# Revit family: P500296-009
name_source: partatom
category: Lighting Fixtures
units: mm (PartAtom-declared; Revit-internal decimal feet)

## family parameters
Cut with Voids When Loaded = No
Host = Face
Light Source = No
OmniClass Number = 23.80.70.11.14.17
OmniClass Title = Direct/Indirect
Part Type = Normal
Room Calculation Point = No
Round Connector Dimension = Use Diameter
Shared = Yes

## types (1)
- P500296-009
    Apparent Load = 60 VA
    Assembly Code = D5020200
    Connector Description = Lighting Connector
    Default Elevation = 48 "
    Description = Vinings Collection Three-Light Brushed Nickel and Grey Washed Oak Foyer Pendant Light
    Features = Application: Add a touch of casual charm with the Vinings Collection 3-Light Brushed Nickel Coastal Foyer Pendant Light ideal for any foyer, dining room, stairway, or entryway.
Styles: Perfect for farmhouse, coastal, and transitional style settings.
Finish: The chic frame with graceful curving arms is coated in a beautiful brushed nickel finish accented by an ornamental, hand-painted gray washed oak faux wood band.
Materials: Constructed from steel to ensure a long product lifespan.
Glass/Shades: Light sources gather at the center for airy illumination.
Bulbs: For ideal illumination, use 3 candelabra base bulbs that are sold separately (60w max - LED/CFL/incandescent). Compatible with dimmable bulbs.
Dimensions: Measures 15-3/4-inch diameter by 19-1/2-inch height.
Certifications: cETLus dry location listed.
Pairs With: Pairs with the Austelle and Winslett collections from Progress Lighting.
Warranty: Our 1-Year Limited Warranty guarantees your complete satisfaction with your purchase and includes professional after-sales customer service support.
    Fixture distribution = Direct
    Glass = Glass - Hubbell - Glass
    Gold = Hubbell - Gold
    Height = 19.5 "
    Housing Material = Hubbell Nickel
    Lamp = LED/CFL/incandescent
    Load Classification = Lighting
    Manufacturer = Progress Lighting
    Model = P500296-009
    Power Factor = 1
    Product Documentation Link = https://hubbellcdn.com
    Product Link = https://www.hubbell.com
    Reflector = Glass - Hubbell - Glass
    Texture = Hubbell Textured Wood
    URL = https://www.hubbell.com
    Voltage = 120 V
    Warranty = 1 year Warranty
    Wattage Comments = 60W
    Watts = 60 W
    Width = 15.75 "

## geometry (parser evidence)
native form markers: Sweep x7
no freeform markers — native parametric forms only
